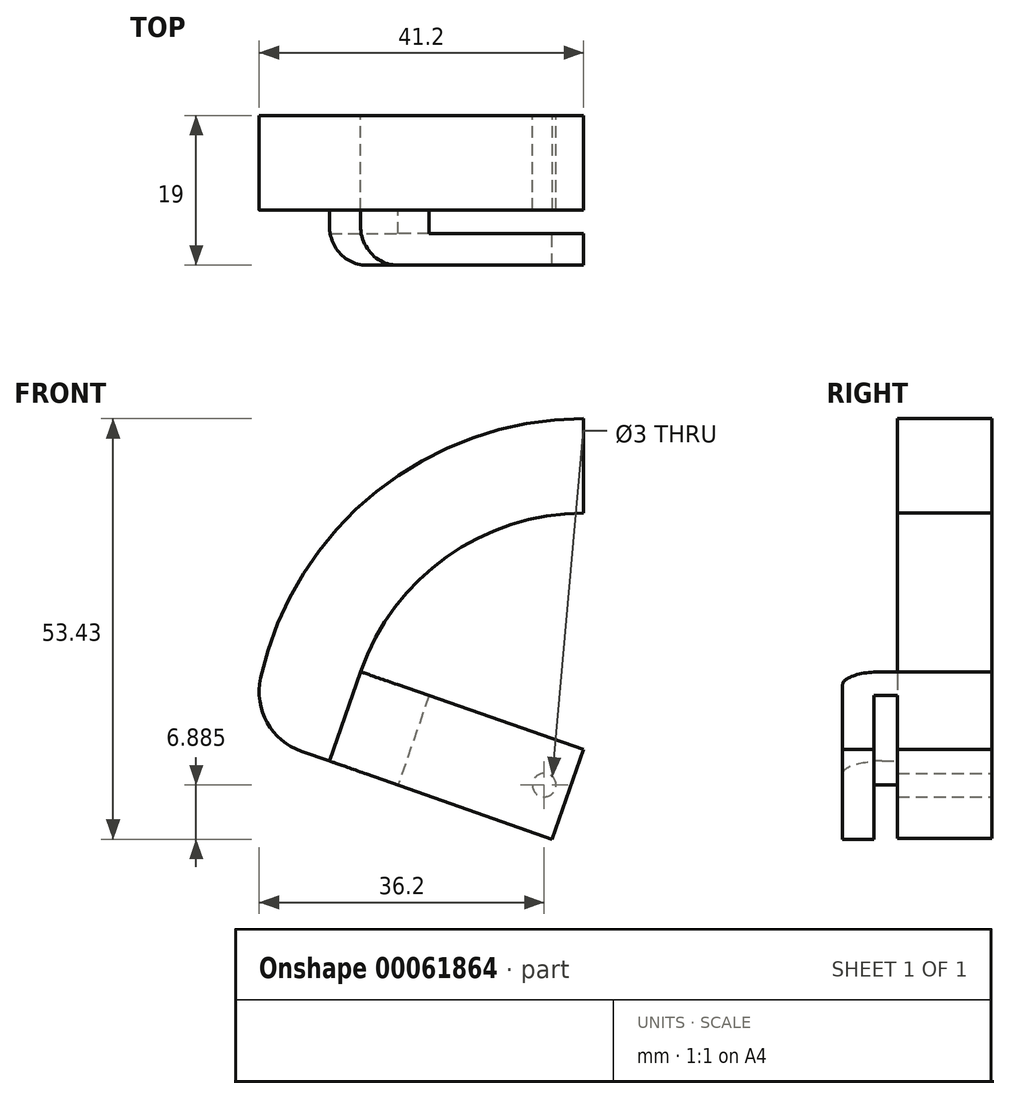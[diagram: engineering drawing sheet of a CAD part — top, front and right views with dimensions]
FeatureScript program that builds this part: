
annotation { "Feature Type Name" : "Feature", "Feature Type Description" : "" }
export const myFeature = defineFeature(function(context is Context, id is Id, definition is map)
    precondition{}
    {
        {
            var Q0;
            Q0=qCreatedBy(makeId("Front.planeOp"),FACE);
            var sketch = newSketch(context, id + "F0", { "sketchPlane" : qUnion([Q0])});
            skArc(sketch, "E0", {"start": v(0, 30) * mm, "mid": v(-17.38, 24.45) * mm, "end": v(-28.33, 9.86) * mm});
            skArc(sketch, "E1", {"start": v(0, 42) * mm, "mid": v(-29.02, 30.36) * mm, "end": v(-41.96, 1.89) * mm});
            skLineSegment(sketch, "E2", {"start": v(0, 30) * mm, "end": v(0, 42) * mm});
            skLineSegment(sketch, "E3", {"start": v(-28.33, 9.86) * mm, "end": v(0, 0) * mm});
            skLineSegment(sketch, "E4", {"start": v(-41.96, 1.89) * mm, "end": v(-3.94, -11.33) * mm});
            skLineSegment(sketch, "E5", {"start": v(-3.94, -11.33) * mm, "end": v(0, 0) * mm});
            skCircle(sketch, "E6", {"center": v(-5, -4.55) * mm, "radius": 1.5 * mm});
            skLineSegment(sketch, "E7", {"start": v(0, 0) * mm, "end": v(-56.95, 0) * mm, "construction": true});
            skSolve(sketch);
        }
        {
            var Q0;
            Q0=makeQuery(id+"F0.imprint","IMPRINT",FACE,{"disambiguationData":[TD([[makeQuery(id+"F0.imprint","IMPRINT",EDGE,{"derivedFrom":sQuery(id+"F0.wireOp",EDGE,"E0")}),-1.0]])]});
            extrude(context, id + "F1", {"entities" : qUnion([Q0]), "endBound" : BoundingType.SYMMETRIC, "depth" : 12 * mm});
        }
        {
            var Q0;
            Q0=makeQuery(id+"F1.opExtrude","CAP_FACE",FACE,{"disambiguationData":[OSD([sQuery(id+"F0.wireOp",EDGE,"E0"),sQuery(id+"F0.wireOp",EDGE,"E1"),sQuery(id+"F0.wireOp",EDGE,"E2"),sQuery(id+"F0.wireOp",EDGE,"E3"),sQuery(id+"F0.wireOp",EDGE,"E4"),sQuery(id+"F0.wireOp",EDGE,"E5"),sQuery(id+"F0.wireOp",EDGE,"E6")])],"isStart":false});
            var sketch = newSketch(context, id + "F2", { "sketchPlane" : qUnion([Q0])});
            skLineSegment(sketch, "E8", {"start": v(-28.33, 9.86) * mm, "end": v(-19.62, 6.82) * mm});
            skLineSegment(sketch, "E9", {"start": v(-19.62, 6.82) * mm, "end": v(-23.56, -4.51) * mm});
            skLineSegment(sketch, "E10", {"start": v(-23.56, -4.51) * mm, "end": v(-32.29, -1.48) * mm});
            skLineSegment(sketch, "E11", {"start": v(-32.29, -1.48) * mm, "end": v(-28.33, 9.86) * mm});
            skSolve(sketch);
        }
        {
            var Q0;
            Q0=makeQuery(id+"F2.imprint","IMPRINT",FACE,{"disambiguationData":[TD([[makeQuery(id+"F2.imprint","IMPRINT",EDGE,{"derivedFrom":sQuery(id+"F2.wireOp",EDGE,"E8")}),-1.0]])]});
            extrude(context, id + "F3", {"entities" : qUnion([Q0]), "operationType" : NewBodyOperationType.ADD, "depth" : 3 * mm});
        }
        {
            var Q0;
            Q0=makeQuery(id+"F3.opExtrude","CAP_FACE",FACE,{"disambiguationData":[OSD([sQuery(id+"F2.wireOp",EDGE,"E8"),sQuery(id+"F2.wireOp",EDGE,"E9"),sQuery(id+"F2.wireOp",EDGE,"E10"),sQuery(id+"F2.wireOp",EDGE,"E11")])],"isStart":false});
            var sketch = newSketch(context, id + "F4", { "sketchPlane" : qUnion([Q0])});
            skLineSegment(sketch, "E12", {"start": v(-28.33, 9.86) * mm, "end": v(0, 0) * mm});
            skLineSegment(sketch, "E13", {"start": v(0, 0) * mm, "end": v(-3.98, -11.43) * mm});
            skLineSegment(sketch, "E14", {"start": v(-3.98, -11.43) * mm, "end": v(-32.29, -1.48) * mm});
            skLineSegment(sketch, "E15", {"start": v(-32.29, -1.48) * mm, "end": v(-28.33, 9.86) * mm});
            skSolve(sketch);
        }
        {
            var Q0;
            Q0 = qSketchRegion(id + "F4", true);
            extrude(context, id + "F5", {"entities" : qUnion([Q0]), "operationType" : NewBodyOperationType.ADD, "depth" : 4 * mm});
        }
        {
            var Q0;
            Q0=makeQuery(id+"F1.opExtrude","SWEPT_EDGE",EDGE,{"disambiguationData":[OSD([sQuery(id+"F0.wireOp",EDGE,"E1"),sQuery(id+"F0.wireOp",EDGE,"E4")])]});
            fillet(context, id + "F6", {"entities" : qUnion([Q0]), "radius" : 8 * mm, "tangentPropagation" : true, "allowEdgeOverflow" : false});
        }
        {
            var Q0;
            Q0=makeQuery(id+"F5.opExtrude","CAP_EDGE",EDGE,{"disambiguationData":[OSD([sQuery(id+"F4.wireOp",EDGE,"E15")])],"isStart":false});
            fillet(context, id + "F7", {"entities" : qUnion([Q0]), "radius" : 5 * mm, "tangentPropagation" : true, "allowEdgeOverflow" : false});
        }
    });
